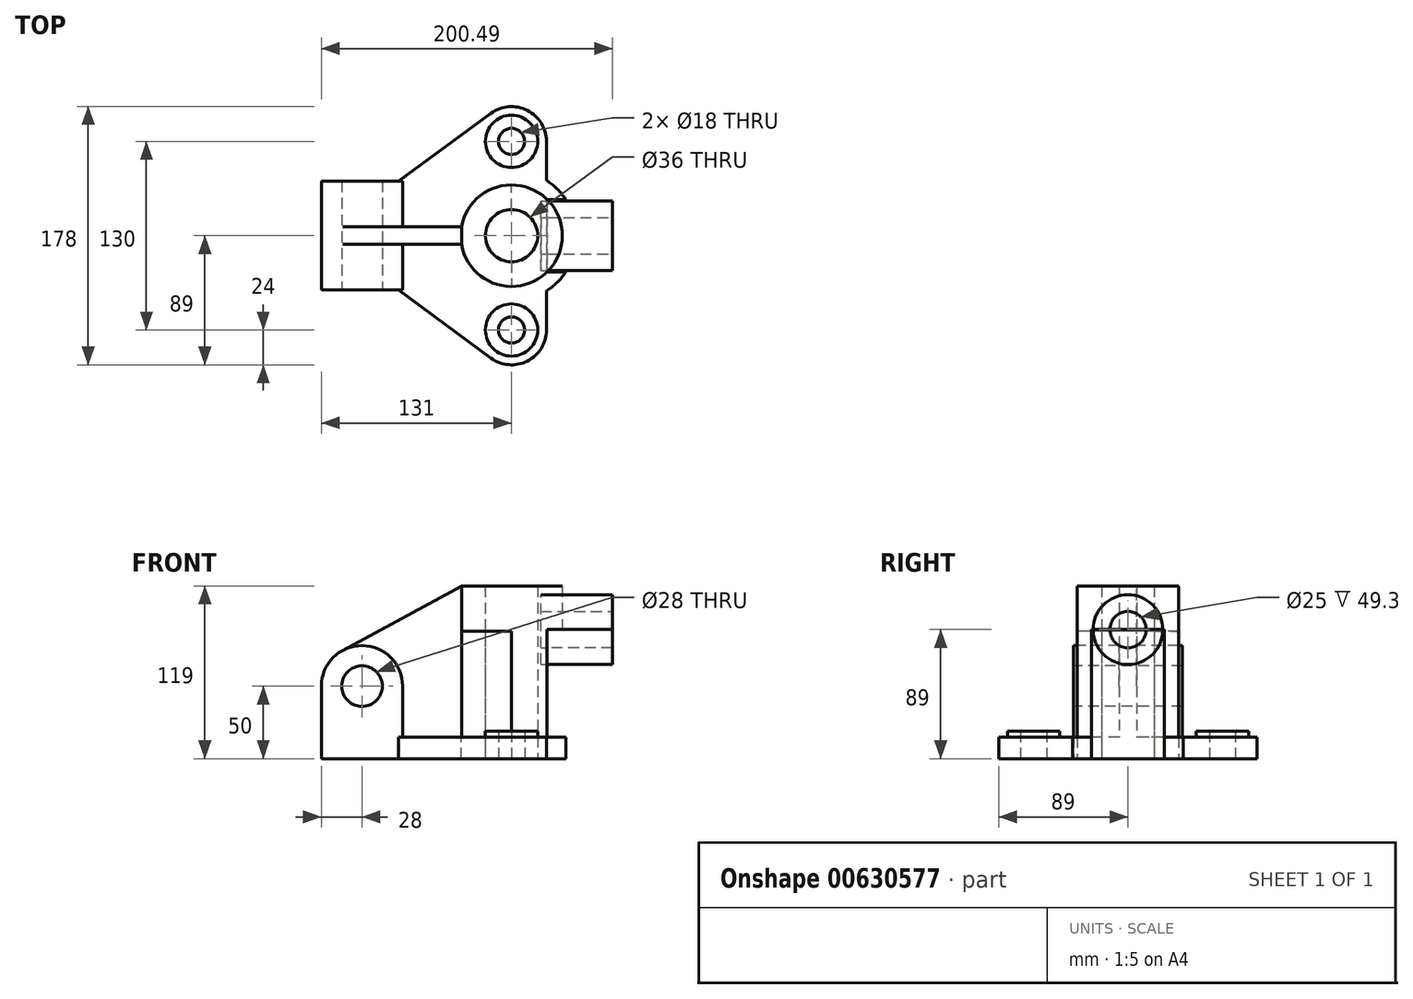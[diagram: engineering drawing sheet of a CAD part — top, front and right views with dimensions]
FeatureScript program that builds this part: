
annotation { "Feature Type Name" : "Feature", "Feature Type Description" : "" }
export const myFeature = defineFeature(function(context is Context, id is Id, definition is map)
    precondition{}
    {
        {
            var Q0;
            Q0=qCreatedBy(makeId("Top.planeOp"),FACE);
            var sketch = newSketch(context, id + "F0", { "sketchPlane" : qUnion([Q0])});
            skLineSegment(sketch, "E0.bottom", {"start": v(25, 37.5) * mm, "end": v(-25, 37.5) * mm});
            skLineSegment(sketch, "E0.top", {"start": v(25, -37.5) * mm, "end": v(-25, -37.5) * mm});
            skLineSegment(sketch, "E0.left", {"start": v(25, 37.5) * mm, "end": v(25, -37.5) * mm});
            skLineSegment(sketch, "E0.right", {"start": v(-25, 37.5) * mm, "end": v(-25, -37.5) * mm});
            skPoint(sketch, "E0.middle", {"position": v(0, 0) * mm});
            skCircle(sketch, "E1", {"center": v(103, 0) * mm, "radius": 35 * mm});
            skPoint(sketch, "E1.centerSnap0", {"position": v(25, 0) * mm});
            skLineSegment(sketch, "E2", {"start": v(103, 0) * mm, "end": v(103, 35) * mm});
            skCircle(sketch, "E3", {"center": v(103, 65) * mm, "radius": 18 * mm});
            skCircle(sketch, "E4", {"center": v(103, 65) * mm, "radius": 9 * mm});
            skCircle(sketch, "E5", {"center": v(103, -65) * mm, "radius": 18 * mm});
            skCircle(sketch, "E6", {"center": v(103, -65) * mm, "radius": 9 * mm});
            skArc(sketch, "E7", {"start": v(127, 65) * mm, "mid": v(113.84, 86.41) * mm, "end": v(88.8, 84.34) * mm});
            skLineSegment(sketch, "E8", {"start": v(25, 37.5) * mm, "end": v(88.8, 84.34) * mm});
            skArc(sketch, "E9", {"start": v(88.8, -84.34) * mm, "mid": v(113.84, -86.41) * mm, "end": v(127, -65) * mm});
            skLineSegment(sketch, "E10", {"start": v(25, -37.5) * mm, "end": v(88.8, -84.34) * mm});
            skArc(sketch, "E11", {"start": v(127, -38.07) * mm, "mid": v(134.4, -32.24) * mm, "end": v(140.42, -25) * mm});
            skLineSegment(sketch, "E12.trimOffspring", {"start": v(103, 35) * mm, "end": v(103, -35) * mm});
            skLineSegment(sketch, "E13", {"start": v(127, -65) * mm, "end": v(127, -38.07) * mm});
            skLineSegment(sketch, "E14", {"start": v(127, 65) * mm, "end": v(127, 38.07) * mm});
            skPoint(sketch, "E15.start.orphan", {"position": v(148, 0) * mm});
            skCircle(sketch, "E16", {"center": v(103, 0) * mm, "radius": 18 * mm});
            skLineSegment(sketch, "E17", {"start": v(148, 25) * mm, "end": v(127.5, 25) * mm});
            skLineSegment(sketch, "E18", {"start": v(148, -25) * mm, "end": v(127.5, -25) * mm});
            skArc(sketch, "E19.trimOffspring", {"start": v(140.42, 25) * mm, "mid": v(134.4, 32.24) * mm, "end": v(127, 38.07) * mm});
            skLineSegment(sketch, "E20", {"start": v(127.5, 25) * mm, "end": v(172.5, 25) * mm});
            skLineSegment(sketch, "E21", {"start": v(172.5, 25) * mm, "end": v(172.5, -25) * mm});
            skLineSegment(sketch, "E22", {"start": v(172.5, -25) * mm, "end": v(148, -25) * mm});
            skSolve(sketch);
        }
        {
            var Q0;
            Q0=makeQuery(id+"F0.imprint","IMPRINT",FACE,{"disambiguationData":[TD([[makeQuery(id+"F0.imprint","IMPRINT",EDGE,{"derivedFrom":sQuery(id+"F0.wireOp",EDGE,"E0.left")}),1.0]])]});
            extrude(context, id + "F1", {"entities" : qUnion([Q0]), "depth" : 15 * mm, "offsetDistance" : 25 * mm});
        }
        {
            var Q0;
            Q0=makeQuery(id+"F0.imprint","IMPRINT",FACE,{"disambiguationData":[TD([[makeQuery(id+"F0.imprint","IMPRINT",EDGE,{"derivedFrom":sQuery(id+"F0.wireOp",EDGE,"E3")}),1.0]])]});
            var Q1;
            Q1=makeQuery(id+"F0.imprint","IMPRINT",FACE,{"disambiguationData":[TD([[makeQuery(id+"F0.imprint","IMPRINT",EDGE,{"derivedFrom":sQuery(id+"F0.wireOp",EDGE,"E5")}),1.0]])]});
            extrude(context, id + "F2", {"entities" : qUnion([Q0, Q1]), "operationType" : NewBodyOperationType.ADD, "depth" : 19 * mm, "offsetDistance" : 25 * mm});
        }
        {
            var Q0;
            {var subQ0=sQuery(id+"F0.wireOp",EDGE,"E12.trimOffspring");var subQ1=sQuery(id+"F0.wireOp",EDGE,"E1");var subQ2=makeQuery(id+"F0.imprint","INTERSECT",VERTEX,{"disambiguationData":[OD(0.0)],"derivedFrom":[subQ1,subQ0]});Q0=makeQuery(id+"F0.imprint","IMPRINT",FACE,{"disambiguationData":[TD([[makeQuery(id+"F0.imprint","IMPRINT",EDGE,{"disambiguationData":[TD([[subQ2,1.0]])],"derivedFrom":subQ1}),1.0]])]});}
            var Q1;
            {var subQ0=sQuery(id+"F0.wireOp",EDGE,"E12.trimOffspring");var subQ1=sQuery(id+"F0.wireOp",EDGE,"E1");var subQ2=makeQuery(id+"F0.imprint","INTERSECT",VERTEX,{"disambiguationData":[OD(0.0)],"derivedFrom":[subQ1,subQ0]});Q1=makeQuery(id+"F0.imprint","IMPRINT",FACE,{"disambiguationData":[TD([[makeQuery(id+"F0.imprint","IMPRINT",EDGE,{"disambiguationData":[TD([[subQ2,-1.0]])],"derivedFrom":subQ1}),1.0]])]});}
            extrude(context, id + "F3", {"entities" : qUnion([Q0, Q1]), "operationType" : NewBodyOperationType.ADD, "depth" : 119 * mm, "offsetDistance" : 25 * mm});
        }
        {
            var Q0;
            Q0=makeQuery(id+"F0.imprint","IMPRINT",FACE,{"disambiguationData":[TD([[makeQuery(id+"F0.imprint","IMPRINT",EDGE,{"derivedFrom":sQuery(id+"F0.wireOp",EDGE,"E0.bottom")}),1.0]])]});
            extrude(context, id + "F4", {"entities" : qUnion([Q0]), "operationType" : NewBodyOperationType.ADD, "depth" : 15 * mm, "offsetDistance" : 25 * mm});
        }
        {
            var Q0;
            Q0=makeQuery(id+"F4.opExtrude","SWEPT_FACE",FACE,{"disambiguationData":[OSD([sQuery(id+"F0.wireOp",EDGE,"E0.top")])]});
            var sketch = newSketch(context, id + "F5", { "sketchPlane" : qUnion([Q0])});
            skLineSegment(sketch, "E23", {"start": v(0, 0) * mm, "end": v(0, 50) * mm});
            skPoint(sketch, "E23.endSnap0", {"position": v(0, 0) * mm});
            skCircle(sketch, "E24", {"center": v(0, 50) * mm, "radius": 14 * mm});
            skCircle(sketch, "E25", {"center": v(0, 50) * mm, "radius": 28 * mm});
            skLineSegment(sketch, "E26", {"start": v(-28, 50) * mm, "end": v(-28, 0) * mm});
            skLineSegment(sketch, "E27", {"start": v(-28, 0) * mm, "end": v(-25, 0) * mm});
            skLineSegment(sketch, "E28", {"start": v(-25, 15) * mm, "end": v(-28, 15) * mm});
            skLineSegment(sketch, "E29", {"start": v(28, 50) * mm, "end": v(28, 0) * mm});
            skLineSegment(sketch, "E30", {"start": v(28, 0) * mm, "end": v(-28, 0) * mm});
            skSolve(sketch);
        }
        {
            var Q0;
            {var subQ0=sQuery(id+"F5.wireOp",EDGE,"E27");Q0=makeQuery(id+"F5.imprint","IMPRINT",FACE,{"disambiguationData":[TD([[makeQuery(id+"F5.imprint","IMPRINT",EDGE,{"derivedFrom":subQ0}),1.0]])]});}
            extrude(context, id + "F6", {"entities" : qUnion([Q0]), "operationType" : NewBodyOperationType.ADD, "oppositeDirection" : true, "depth" : 75 * mm, "offsetDistance" : 25 * mm});
        }
        {
            var Q0;
            Q0=makeQuery(id+"F5.imprint","IMPRINT",FACE,{"disambiguationData":[TD([[makeQuery(id+"F5.imprint","IMPRINT",EDGE,{"derivedFrom":sQuery(id+"F5.wireOp",EDGE,"E24")}),-1.0]])]});
            var Q1;
            {var subQ0=sQuery(id+"F5.wireOp",EDGE,"E28");Q1=makeQuery(id+"F5.imprint","IMPRINT",FACE,{"disambiguationData":[TD([[makeQuery(id+"F5.imprint","IMPRINT",EDGE,{"derivedFrom":subQ0}),-1.0]])]});}
            extrude(context, id + "F7", {"entities" : qUnion([Q0, Q1]), "operationType" : NewBodyOperationType.ADD, "oppositeDirection" : true, "depth" : 75 * mm, "offsetDistance" : 25 * mm});
        }
        {
            var Q0;
            {var subQ0=sQuery(id+"F5.wireOp",EDGE,"E29");Q0=makeQuery(id+"F5.imprint","IMPRINT",FACE,{"disambiguationData":[TD([[makeQuery(id+"F5.imprint","IMPRINT",EDGE,{"derivedFrom":subQ0}),-1.0]])]});}
            extrude(context, id + "F8", {"entities" : qUnion([Q0]), "operationType" : NewBodyOperationType.ADD, "oppositeDirection" : true, "depth" : 75 * mm, "offsetDistance" : 25 * mm});
        }
        {
            var Q0;
            {var subQ0=sQuery(id+"F0.wireOp",EDGE,"E0.left");Q0=makeQuery(id+"F4.boolean.opBoolean","MERGE",FACE,{"derivedFrom":[makeQuery(id+"F1.opExtrude","CAP_FACE",FACE,{"disambiguationData":[OSD([subQ0,sQuery(id+"F0.wireOp",EDGE,"E1"),sQuery(id+"F0.wireOp",EDGE,"E3"),sQuery(id+"F0.wireOp",EDGE,"E5"),sQuery(id+"F0.wireOp",EDGE,"E7"),sQuery(id+"F0.wireOp",EDGE,"E8"),sQuery(id+"F0.wireOp",EDGE,"E9"),sQuery(id+"F0.wireOp",EDGE,"E10"),sQuery(id+"F0.wireOp",EDGE,"E11"),sQuery(id+"F0.wireOp",EDGE,"E13"),sQuery(id+"F0.wireOp",EDGE,"E14"),sQuery(id+"F0.wireOp",EDGE,"E18"),sQuery(id+"F0.wireOp",EDGE,"E19.trimOffspring"),sQuery(id+"F0.wireOp",EDGE,"E20")])],"isStart":false}),makeQuery(id+"F4.opExtrude","CAP_FACE",FACE,{"disambiguationData":[OSD([sQuery(id+"F0.wireOp",EDGE,"E0.bottom"),sQuery(id+"F0.wireOp",EDGE,"E0.top"),subQ0,sQuery(id+"F0.wireOp",EDGE,"E0.right")])],"isStart":false})]});}
            var sketch = newSketch(context, id + "F9", { "sketchPlane" : qUnion([Q0])});
            skLineSegment(sketch, "E31", {"start": v(28, 0) * mm, "end": v(28, -6) * mm});
            skLineSegment(sketch, "E32", {"start": v(28, -6) * mm, "end": v(28, 6) * mm});
            skLineSegment(sketch, "E33", {"start": v(28, 6) * mm, "end": v(68.52, 6) * mm});
            skLineSegment(sketch, "E34", {"start": v(28, -6) * mm, "end": v(68.52, -6) * mm});
            skSolve(sketch);
        }
        {
            var Q0;
            Q0 = qSketchRegion(id + "F9", true);
            var Q1;
            {var subQ0=sQuery(id+"F9.wireOp",EDGE,"E33");Q1=makeQuery(id+"F9.imprint","IMPRINT",FACE,{"disambiguationData":[TD([[makeQuery(id+"F9.imprint","IMPRINT",EDGE,{"derivedFrom":subQ0}),-1.0]])]});}
            extrude(context, id + "F10", {"entities" : qUnion([Q0, Q1]), "operationType" : NewBodyOperationType.ADD, "depth" : 104 * mm, "offsetDistance" : 25 * mm});
        }
        {
            var Q0;
            Q0=makeQuery(id+"F10.opExtrude","SWEPT_FACE",FACE,{"disambiguationData":[OSD([sQuery(id+"F9.wireOp",EDGE,"E32")])]});
            extrude(context, id + "F11", {"entities" : qUnion([Q0]), "operationType" : NewBodyOperationType.ADD, "depth" : 60 * mm, "offsetDistance" : 25 * mm});
        }
        {
            var Q0;
            {var subQ0=sQuery(id+"F9.wireOp",EDGE,"E34");Q0=makeQuery(id+"F11.boolean.opBoolean","MERGE",FACE,{"derivedFrom":[makeQuery(id+"F10.opExtrude","SWEPT_FACE",FACE,{"disambiguationData":[OSD([subQ0])]}),makeQuery(id+"F11.opExtrude","SWEPT_FACE",FACE,{"disambiguationData":[OSD([sQuery(id+"F0.wireOp",EDGE,"E0.bottom"),sQuery(id+"F0.wireOp",EDGE,"E0.top"),sQuery(id+"F0.wireOp",EDGE,"E0.left"),sQuery(id+"F0.wireOp",EDGE,"E0.right"),sQuery(id+"F0.wireOp",EDGE,"E1"),sQuery(id+"F0.wireOp",EDGE,"E3"),sQuery(id+"F0.wireOp",EDGE,"E5"),sQuery(id+"F0.wireOp",EDGE,"E7"),sQuery(id+"F0.wireOp",EDGE,"E8"),sQuery(id+"F0.wireOp",EDGE,"E9"),sQuery(id+"F0.wireOp",EDGE,"E10"),sQuery(id+"F0.wireOp",EDGE,"E11"),sQuery(id+"F0.wireOp",EDGE,"E13"),sQuery(id+"F0.wireOp",EDGE,"E14"),sQuery(id+"F0.wireOp",EDGE,"E18"),sQuery(id+"F0.wireOp",EDGE,"E19.trimOffspring"),sQuery(id+"F0.wireOp",EDGE,"E20"),sQuery(id+"F5.wireOp",EDGE,"E29"),sQuery(id+"F9.wireOp",EDGE,"E32"),subQ0])]})]});}
            var sketch = newSketch(context, id + "F12", { "sketchPlane" : qUnion([Q0])});
            skLineSegment(sketch, "E35", {"start": v(68.52, 119) * mm, "end": v(-13.35, 74.61) * mm});
            skSolve(sketch);
        }
        {
            var Q0;
            {var subQ23=sQuery(id+"F12.wireOp",EDGE,"E35");Q0=makeQuery(id+"F12.imprint","IMPRINT",FACE,{"disambiguationData":[TD([[makeQuery(id+"F12.imprint","IMPRINT",EDGE,{"derivedFrom":subQ23}),-1.0]])]});}
            var Q1;
            Q1=makeQuery(id+"F11.boolean.opBoolean","SPLIT",FACE,{"derivedFrom":makeQuery(id+"F11.opExtrude","SWEPT_FACE",FACE,{"disambiguationData":[OSD([sQuery(id+"F0.wireOp",EDGE,"E0.bottom"),sQuery(id+"F0.wireOp",EDGE,"E0.top"),sQuery(id+"F0.wireOp",EDGE,"E0.left"),sQuery(id+"F0.wireOp",EDGE,"E0.right"),sQuery(id+"F0.wireOp",EDGE,"E1"),sQuery(id+"F0.wireOp",EDGE,"E3"),sQuery(id+"F0.wireOp",EDGE,"E5"),sQuery(id+"F0.wireOp",EDGE,"E7"),sQuery(id+"F0.wireOp",EDGE,"E8"),sQuery(id+"F0.wireOp",EDGE,"E9"),sQuery(id+"F0.wireOp",EDGE,"E10"),sQuery(id+"F0.wireOp",EDGE,"E11"),sQuery(id+"F0.wireOp",EDGE,"E13"),sQuery(id+"F0.wireOp",EDGE,"E14"),sQuery(id+"F0.wireOp",EDGE,"E18"),sQuery(id+"F0.wireOp",EDGE,"E19.trimOffspring"),sQuery(id+"F0.wireOp",EDGE,"E20"),sQuery(id+"F5.wireOp",EDGE,"E29"),sQuery(id+"F9.wireOp",EDGE,"E32"),sQuery(id+"F9.wireOp",EDGE,"E33")])]})});
            extrude(context, id + "F13", {"entities" : qUnion([Q0, Q1]), "operationType" : NewBodyOperationType.REMOVE, "oppositeDirection" : true, "depth" : 25 * mm, "offsetDistance" : 25 * mm});
        }
        {
            var Q0;
            Q0=makeQuery(id+"F11.boolean.opBoolean","SPLIT",FACE,{"derivedFrom":makeQuery(id+"F11.opExtrude","SWEPT_FACE",FACE,{"disambiguationData":[OSD([sQuery(id+"F0.wireOp",EDGE,"E0.bottom"),sQuery(id+"F0.wireOp",EDGE,"E0.top"),sQuery(id+"F0.wireOp",EDGE,"E0.left"),sQuery(id+"F0.wireOp",EDGE,"E0.right"),sQuery(id+"F0.wireOp",EDGE,"E1"),sQuery(id+"F0.wireOp",EDGE,"E3"),sQuery(id+"F0.wireOp",EDGE,"E5"),sQuery(id+"F0.wireOp",EDGE,"E7"),sQuery(id+"F0.wireOp",EDGE,"E8"),sQuery(id+"F0.wireOp",EDGE,"E9"),sQuery(id+"F0.wireOp",EDGE,"E10"),sQuery(id+"F0.wireOp",EDGE,"E11"),sQuery(id+"F0.wireOp",EDGE,"E13"),sQuery(id+"F0.wireOp",EDGE,"E14"),sQuery(id+"F0.wireOp",EDGE,"E18"),sQuery(id+"F0.wireOp",EDGE,"E19.trimOffspring"),sQuery(id+"F0.wireOp",EDGE,"E20"),sQuery(id+"F5.wireOp",EDGE,"E29"),sQuery(id+"F9.wireOp",EDGE,"E32"),sQuery(id+"F9.wireOp",EDGE,"E33")])]})});
            var sketch = newSketch(context, id + "F14", { "sketchPlane" : qUnion([Q0])});
            skSolve(sketch);
        }
        {
            var Q0;
            Q0 = qSketchRegion(id + "F14", true);
            var Q1;
            {var subQ0=sQuery(id+"F9.wireOp",EDGE,"E33");var subQ1=sQuery(id+"F9.wireOp",EDGE,"E32");var subQ2=sQuery(id+"F5.wireOp",EDGE,"E29");var subQ3=makeQuery(id+"F11.opExtrude","SWEPT_FACE",FACE,{"disambiguationData":[OSD([sQuery(id+"F0.wireOp",EDGE,"E0.bottom"),sQuery(id+"F0.wireOp",EDGE,"E0.top"),sQuery(id+"F0.wireOp",EDGE,"E0.left"),sQuery(id+"F0.wireOp",EDGE,"E0.right"),sQuery(id+"F0.wireOp",EDGE,"E1"),sQuery(id+"F0.wireOp",EDGE,"E3"),sQuery(id+"F0.wireOp",EDGE,"E5"),sQuery(id+"F0.wireOp",EDGE,"E7"),sQuery(id+"F0.wireOp",EDGE,"E8"),sQuery(id+"F0.wireOp",EDGE,"E9"),sQuery(id+"F0.wireOp",EDGE,"E10"),sQuery(id+"F0.wireOp",EDGE,"E11"),sQuery(id+"F0.wireOp",EDGE,"E13"),sQuery(id+"F0.wireOp",EDGE,"E14"),sQuery(id+"F0.wireOp",EDGE,"E18"),sQuery(id+"F0.wireOp",EDGE,"E19.trimOffspring"),sQuery(id+"F0.wireOp",EDGE,"E20"),subQ2,subQ1,subQ0])]});Q1=makeQuery(id+"F14.imprint","IMPRINT",FACE,{"disambiguationData":[TD([[makeQuery(id+"F14.imprint","IMPRINT",EDGE,{"derivedFrom":makeQuery(id+"F11.boolean.opBoolean","INTERSECT",EDGE,{"derivedFrom":[makeQuery(id+"F7.opExtrude","SWEPT_FACE",FACE,{"disambiguationData":[OSD([sQuery(id+"F5.wireOp",EDGE,"E24")])]}),subQ3]})}),1.0]])]});}
            extrude(context, id + "F15", {"entities" : qUnion([Q0, Q1]), "operationType" : NewBodyOperationType.REMOVE, "oppositeDirection" : true, "depth" : 25 * mm, "offsetDistance" : 25 * mm});
        }
        {
            var Q0;
            {var subQ8=sQuery(id+"F0.wireOp",EDGE,"E21");Q0=makeQuery(id+"F0.imprint","IMPRINT",FACE,{"disambiguationData":[TD([[makeQuery(id+"F0.imprint","IMPRINT",EDGE,{"derivedFrom":subQ8}),-1.0]])]});}
            extrude(context, id + "F16", {"entities" : qUnion([Q0]), "depth" : 89 * mm, "offsetDistance" : 25 * mm});
        }
        {
            var Q0;
            Q0=makeQuery(id+"F16.opExtrude","SWEPT_FACE",FACE,{"disambiguationData":[OSD([sQuery(id+"F0.wireOp",EDGE,"E21")])]});
            var sketch = newSketch(context, id + "F17", { "sketchPlane" : qUnion([Q0])});
            skLineSegment(sketch, "E36", {"start": v(-35, 15) * mm, "end": v(-35, 119) * mm});
            skLineSegment(sketch, "E37", {"start": v(35, 119) * mm, "end": v(35, 15) * mm});
            skLineSegment(sketch, "E38", {"start": v(35, 89) * mm, "end": v(-35, 89) * mm});
            skCircle(sketch, "E39", {"center": v(0, 89) * mm, "radius": 24 * mm});
            skCircle(sketch, "E40", {"center": v(0, 89) * mm, "radius": 12.5 * mm});
            skSolve(sketch);
        }
        {
            var Q0;
            Q0 = qSketchRegion(id + "F17", true);
            extrude(context, id + "F18", {"entities" : qUnion([Q0]), "oppositeDirection" : true, "depth" : 49.3 * mm, "offsetDistance" : 25 * mm});
        }
        {
            var Q0;
            Q0=makeQuery(id+"F16.opExtrude","SWEPT_FACE",FACE,{"disambiguationData":[OSD([sQuery(id+"F0.wireOp",EDGE,"E21")])]});
            extrude(context, id + "F19", {"entities" : qUnion([Q0]), "operationType" : NewBodyOperationType.REMOVE, "oppositeDirection" : true, "depth" : 45 * mm, "offsetDistance" : 25 * mm});
        }
        {
            var Q0;
            {var subQ0=sQuery(id+"F0.wireOp",EDGE,"E21");Q0=makeQuery(id+"F19.boolean.opBoolean","COPY",FACE,{"disambiguationData":[TD([makeQuery(id+"F18.opExtrude","SWEPT_FACE",FACE,{"disambiguationData":[OSD([sQuery(id+"F17.wireOp",EDGE,"E39")])]})])],"derivedFrom":makeQuery(id+"F19.opExtrude","CAP_FACE",FACE,{"disambiguationData":[OSD([subQ0])],"isStart":false})});}
            var sketch = newSketch(context, id + "F20", { "sketchPlane" : qUnion([Q0])});
            skSolve(sketch);
        }
        {
            var Q0;
            Q0 = qSketchRegion(id + "F20", true);
            var Q1;
            {var subQ0=sQuery(id+"F0.wireOp",EDGE,"E21");var subQ1=makeQuery(id+"F19.opExtrude","CAP_FACE",FACE,{"disambiguationData":[OSD([subQ0])],"isStart":false});var subQ2=makeQuery(id+"F18.opExtrude","SWEPT_FACE",FACE,{"disambiguationData":[OSD([sQuery(id+"F17.wireOp",EDGE,"E39")])]});Q1=makeQuery(id+"F20.imprint","IMPRINT",FACE,{"disambiguationData":[TD([[makeQuery(id+"F20.imprint","IMPRINT",EDGE,{"derivedFrom":makeQuery(id+"F19.boolean.opBoolean","INTERSECT",EDGE,{"derivedFrom":[subQ2,subQ1]})}),-1.0]])]});}
            extrude(context, id + "F21", {"entities" : qUnion([Q0, Q1]), "depth" : 45 * mm, "offsetDistance" : 25 * mm});
        }
        {
            var Q0;
            {var subQ0=sQuery(id+"F0.wireOp",EDGE,"E12.trimOffspring");var subQ1=sQuery(id+"F0.wireOp",EDGE,"E1");var subQ2=makeQuery(id+"F0.imprint","INTERSECT",VERTEX,{"disambiguationData":[OD(0.0)],"derivedFrom":[subQ1,subQ0]});Q0=makeQuery(id+"F0.imprint","IMPRINT",FACE,{"disambiguationData":[TD([[makeQuery(id+"F0.imprint","IMPRINT",EDGE,{"disambiguationData":[TD([[subQ2,1.0]])],"derivedFrom":subQ1}),1.0]])]});}
            var sketch = newSketch(context, id + "F22", { "sketchPlane" : qUnion([Q0])});
            skSolve(sketch);
        }
        {
            var Q0;
            Q0 = qSketchRegion(id + "F22", true);
            var Q1;
            {var subQ0=sQuery(id+"F0.wireOp",EDGE,"E12.trimOffspring");var subQ1=sQuery(id+"F0.wireOp",EDGE,"E1");var subQ2=makeQuery(id+"F0.imprint","INTERSECT",VERTEX,{"disambiguationData":[OD(0.0)],"derivedFrom":[subQ1,subQ0]});Q1=makeQuery(id+"F0.imprint","IMPRINT",FACE,{"disambiguationData":[TD([[makeQuery(id+"F0.imprint","IMPRINT",EDGE,{"disambiguationData":[TD([[subQ2,1.0]])],"derivedFrom":subQ1}),1.0]])]});}
            extrude(context, id + "F23", {"entities" : qUnion([Q0, Q1]), "depth" : 88 * mm, "offsetDistance" : 25 * mm});
        }
        {
            var Q0;
            {var subQ3=sQuery(id+"F5.wireOp",EDGE,"E28");Q0=makeQuery(id+"F5.imprint","IMPRINT",FACE,{"disambiguationData":[TD([[makeQuery(id+"F5.imprint","IMPRINT",EDGE,{"derivedFrom":subQ3}),1.0]])]});}
            extrude(context, id + "F24", {"entities" : qUnion([Q0]), "operationType" : NewBodyOperationType.ADD, "oppositeDirection" : true, "depth" : 75 * mm, "offsetDistance" : 25 * mm});
        }
    });
